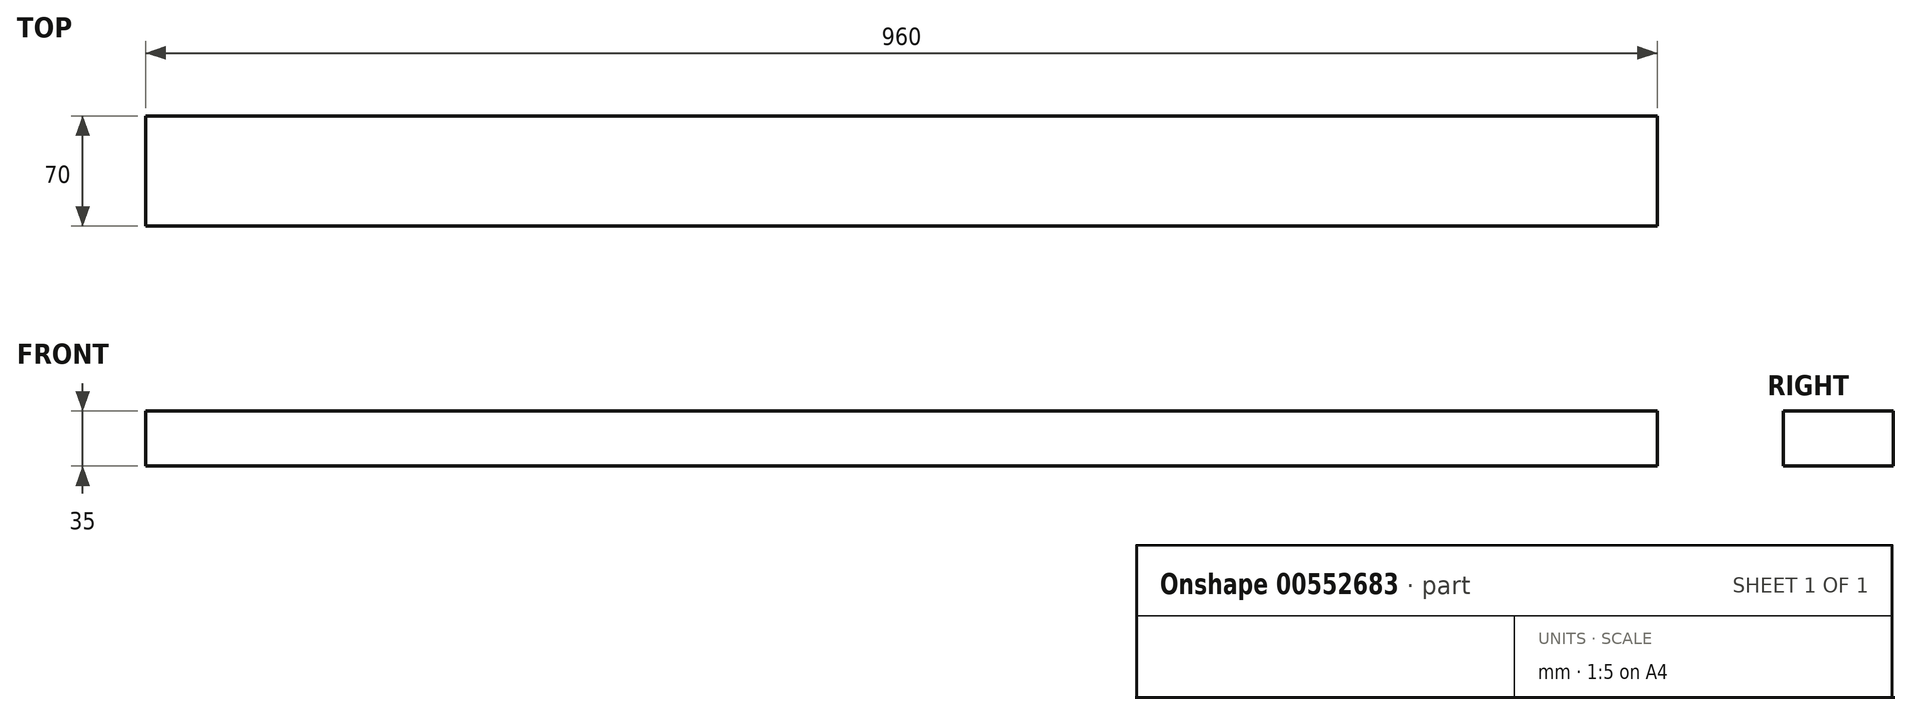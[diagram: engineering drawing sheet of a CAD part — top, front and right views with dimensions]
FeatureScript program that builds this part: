
annotation { "Feature Type Name" : "Feature", "Feature Type Description" : "" }
export const myFeature = defineFeature(function(context is Context, id is Id, definition is map)
    precondition{}
    {
        {
            var Q0;
            Q0=qCreatedBy(makeId("Front.planeOp"),FACE);
            var sketch = newSketch(context, id + "F0", { "sketchPlane" : qUnion([Q0])});
            skLineSegment(sketch, "E0.bottom", {"start": v(480, 17.5) * mm, "end": v(-480, 17.5) * mm});
            skLineSegment(sketch, "E0.top", {"start": v(480, -17.5) * mm, "end": v(-480, -17.5) * mm});
            skLineSegment(sketch, "E0.left", {"start": v(480, 17.5) * mm, "end": v(480, -17.5) * mm});
            skLineSegment(sketch, "E0.right", {"start": v(-480, 17.5) * mm, "end": v(-480, -17.5) * mm});
            skPoint(sketch, "E0.middle", {"position": v(0, 0) * mm});
            skSolve(sketch);
        }
        {
            var Q0;
            Q0 = qSketchRegion(id + "F0", true);
            extrude(context, id + "F1", {"entities" : qUnion([Q0]), "oppositeDirection" : true, "depth" : 70 * mm, "offsetDistance" : 25 * mm});
        }
    });
